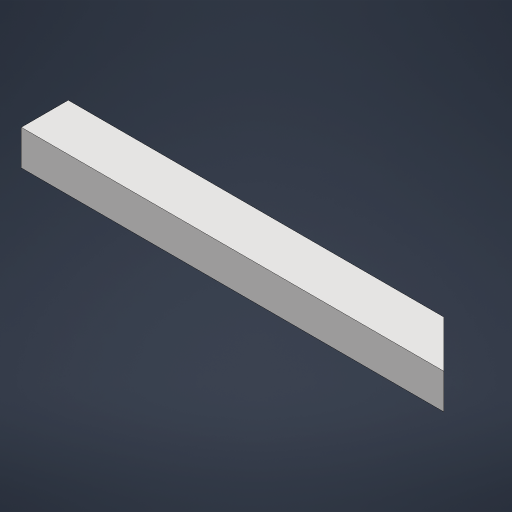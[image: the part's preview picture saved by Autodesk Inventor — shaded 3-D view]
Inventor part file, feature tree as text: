
AUTODESK INVENTOR PART (.ipt)
format: ipt  version: 2023.2 (Build 272271000, 271)  size: 161,280 bytes
history: native  units: in
note: dims shown in document units (in); Inventor stores cm internally (conversion verified against a paired STEP export)
features: extrude x1, sketch x1
ambient origin geometry x8: Origin, YZ Plane, XZ Plane, XY Plane, X Axis, Y Axis, Z Axis, Center Point
bodies: Solid1 (feature_tree)
feature tree (2):
  extrude  "Extrusion1"  Depth=2.0in
  sketch  "Sketch2"  dims[d3=18.0in d4=2.0in d5=45.0deg d6=1.5in d7=0.0in]
